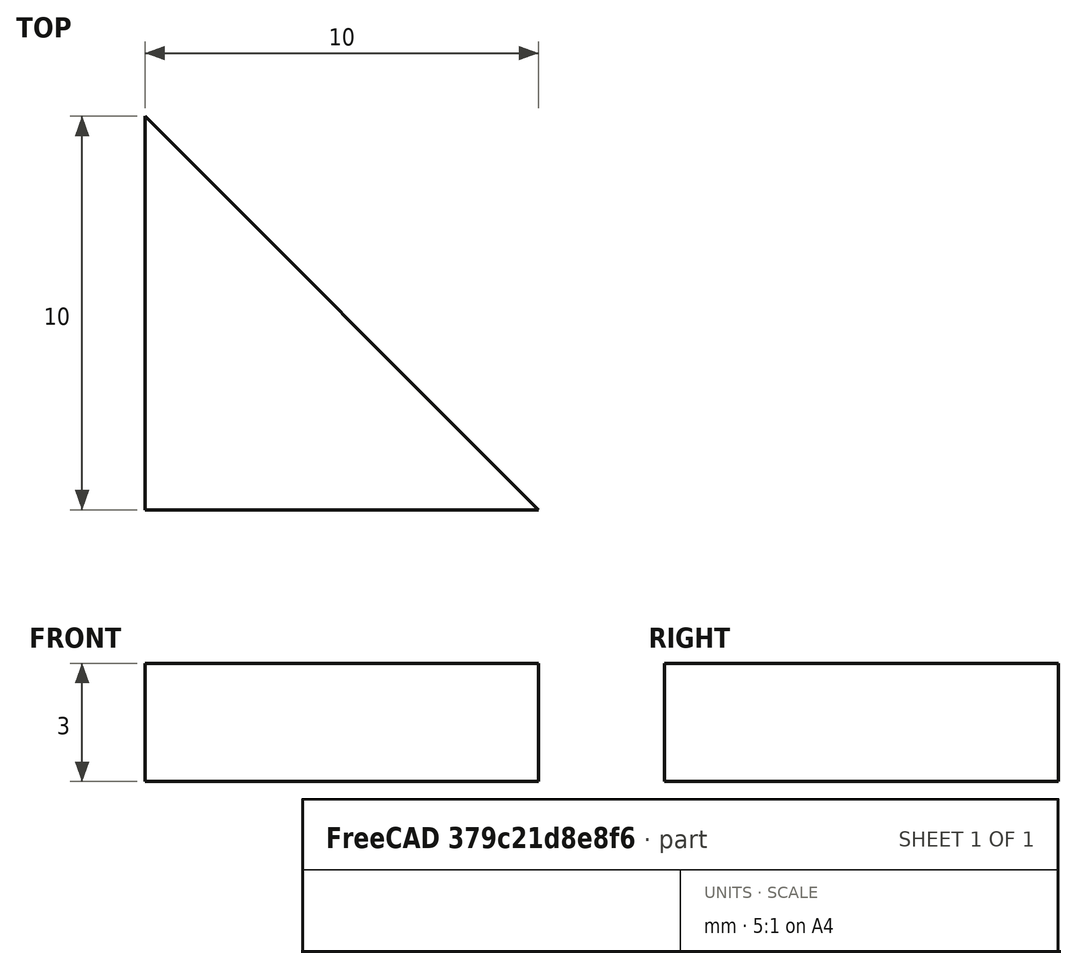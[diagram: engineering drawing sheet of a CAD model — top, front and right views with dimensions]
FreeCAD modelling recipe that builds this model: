
FCSTD DOCUMENT  (FreeCAD 0.19R24276 (Git))
Label: Nemo23_support_front_side
License: All rights reserved
LicenseURL: http://en.wikipedia.org/wiki/All_rights_reserved
objects: Sketcher::SketchObject×1, PartDesign::Pad×1, PartDesign::Body×1
note: 4 computed .brp shape members not serialized (recipe doc carries the construction recipe); baked Part::Feature solids carry a one-line shape summary decoded from their .brp

FEATURE [Sketcher::SketchObject] Sketch
  FullyConstrained = true
  MapMode = 5
  Support = -> [XY_Plane]
  sketch-geometry (3):
    g0: LineSegment StartX=0 StartY=0 StartZ=0 EndX=10 EndY=0 EndZ=0
    g1: LineSegment StartX=0 StartY=0 StartZ=0 EndX=0 EndY=10 EndZ=0
    g2: LineSegment StartX=0 StartY=10 StartZ=0 EndX=10 EndY=0 EndZ=0
  constraints (8):
    c: Coincident(g0,g-1)
    c: PointOnObject(g0,g-1)
    c: Coincident(g1,g0)
    c: PointOnObject(g1,g-2)
    c: Coincident(g2,g1)
    c: Coincident(g2,g0)
    c: DistanceX(g0,g0) = 10
    c: DistanceY(g1,g1) = 10
FEATURE [PartDesign::Pad] Pad
  Direction = (1,1,1)
  Length = 3
  Length2 = 100
  Profile = -> Sketch
  Type = 0
FEATURE [PartDesign::Body] Body
  Group = -> [Sketch,Pad]
  Origin = -> Origin
  Tip = -> Pad
